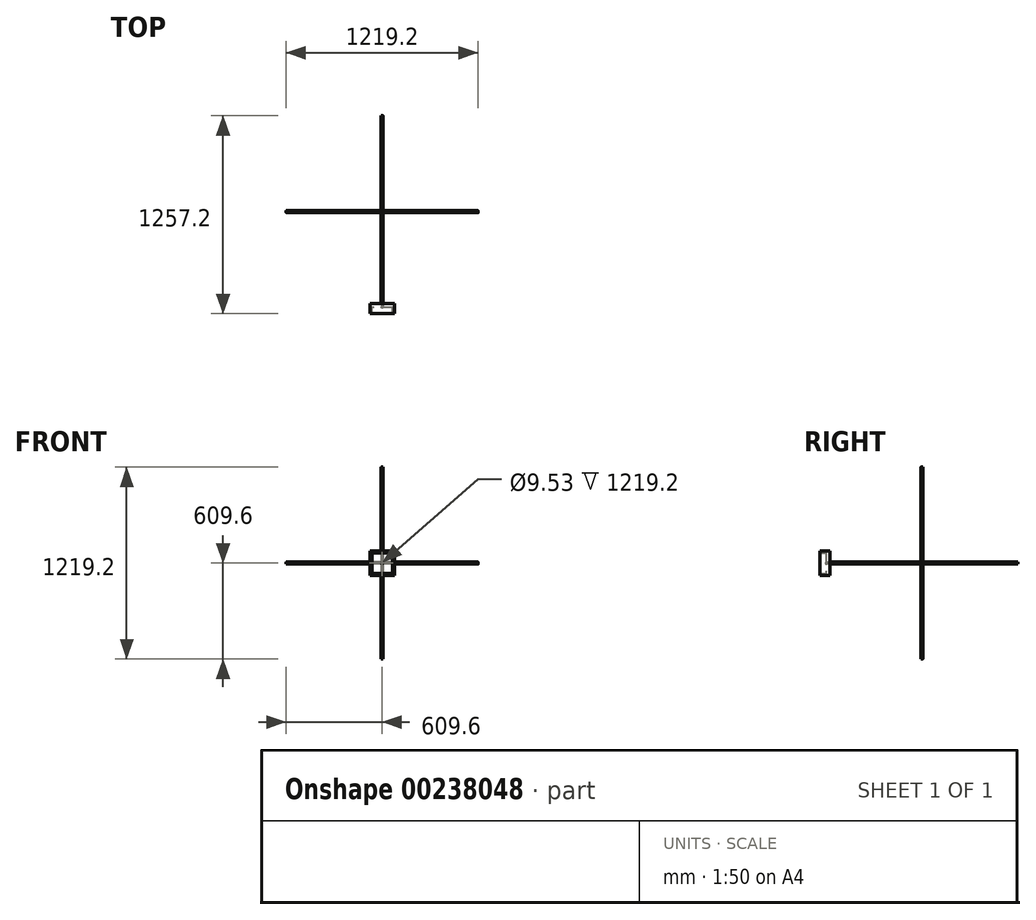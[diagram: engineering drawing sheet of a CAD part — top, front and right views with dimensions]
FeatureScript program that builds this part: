
annotation { "Feature Type Name" : "Feature", "Feature Type Description" : "" }
export const myFeature = defineFeature(function(context is Context, id is Id, definition is map)
    precondition{}
    {
        {
            assignVariable(context, id + "F0", {"name" : "l", "anyValue" : 1219.2 * mm});
        }
        {
            var Q0;
            Q0=qCreatedBy(makeId("Top.planeOp"),FACE);
            var sketch = newSketch(context, id + "F1", { "sketchPlane" : qUnion([Q0])});
            skCircle(sketch, "E0", {"center": v(0, 0) * mm, "radius": 6.35 * mm});
            skSolve(sketch);
        }
        {
            var Q0;
            Q0=qCreatedBy(makeId("Front.planeOp"),FACE);
            var sketch = newSketch(context, id + "F2", { "sketchPlane" : qUnion([Q0])});
            skCircle(sketch, "E1", {"center": v(0, 0) * mm, "radius": 6.35 * mm});
            skSolve(sketch);
        }
        {
            var Q0;
            Q0=qCreatedBy(makeId("Right.planeOp"),FACE);
            var sketch = newSketch(context, id + "F3", { "sketchPlane" : qUnion([Q0])});
            skCircle(sketch, "E2", {"center": v(0, 0) * mm, "radius": 6.35 * mm});
            skSolve(sketch);
        }
        {
            var Q0;
            Q0=makeQuery(id+"F2.imprint","IMPRINT",FACE,{"disambiguationData":[TD([[makeQuery(id+"F2.imprint","IMPRINT",EDGE,{"derivedFrom":sQuery(id+"F2.wireOp",EDGE,"E1")}),1.0]])]});
            extrude(context, id + "F4", {"entities" : qUnion([Q0]), "endBound" : BoundingType.SYMMETRIC, "depth" : getVariable(context, 'l')});
        }
        {
            var Q0;
            Q0=makeQuery(id+"F3.imprint","IMPRINT",FACE,{"disambiguationData":[TD([[makeQuery(id+"F3.imprint","IMPRINT",EDGE,{"derivedFrom":sQuery(id+"F3.wireOp",EDGE,"E2")}),1.0]])]});
            extrude(context, id + "F5", {"entities" : qUnion([Q0]), "operationType" : NewBodyOperationType.ADD, "endBound" : BoundingType.SYMMETRIC, "depth" : getVariable(context, 'l')});
        }
        {
            var Q0;
            Q0=makeQuery(id+"F1.imprint","IMPRINT",FACE,{"disambiguationData":[TD([[makeQuery(id+"F1.imprint","IMPRINT",EDGE,{"derivedFrom":sQuery(id+"F1.wireOp",EDGE,"E0")}),1.0]])]});
            extrude(context, id + "F6", {"entities" : qUnion([Q0]), "operationType" : NewBodyOperationType.ADD, "endBound" : BoundingType.SYMMETRIC, "depth" : getVariable(context, 'l')});
        }
        {
            var Q0;
            Q0=makeQuery(id+"F4.opExtrude","CAP_FACE",FACE,{"disambiguationData":[OSD([sQuery(id+"F2.wireOp",EDGE,"E1")])],"isStart":false});
            var sketch = newSketch(context, id + "F7", { "sketchPlane" : qUnion([Q0])});
            skLineSegment(sketch, "E3.bottom", {"start": v(77.78, 77.78) * mm, "end": v(-77.78, 77.78) * mm});
            skLineSegment(sketch, "E3.top", {"start": v(77.78, -77.78) * mm, "end": v(-77.78, -77.78) * mm});
            skLineSegment(sketch, "E3.left", {"start": v(77.78, 77.78) * mm, "end": v(77.78, -77.78) * mm});
            skLineSegment(sketch, "E3.right", {"start": v(-77.78, 77.78) * mm, "end": v(-77.78, -77.78) * mm});
            skPoint(sketch, "E3.middle", {"position": v(0, 0) * mm});
            skSolve(sketch);
        }
        {
            var Q0;
            Q0 = qSketchRegion(id + "F7", true);
            extrude(context, id + "F8", {"entities" : qUnion([Q0]), "operationType" : NewBodyOperationType.ADD, "oppositeDirection" : true, "depth" : 25.4 * mm});
        }
        {
            var Q0;
            Q0=makeQuery(id+"F8.boolean.opBoolean","MERGE",FACE,{"derivedFrom":[makeQuery(id+"F4.opExtrude","CAP_FACE",FACE,{"disambiguationData":[OSD([sQuery(id+"F2.wireOp",EDGE,"E1")])],"isStart":false}),makeQuery(id+"F8.opExtrude","CAP_FACE",FACE,{"disambiguationData":[OSD([sQuery(id+"F7.wireOp",EDGE,"E3.bottom"),sQuery(id+"F7.wireOp",EDGE,"E3.top"),sQuery(id+"F7.wireOp",EDGE,"E3.left"),sQuery(id+"F7.wireOp",EDGE,"E3.right")])],"isStart":true})]});
            var sketch = newSketch(context, id + "F9", { "sketchPlane" : qUnion([Q0])});
            skLineSegment(sketch, "E4.bottom", {"start": v(65.08, 65.08) * mm, "end": v(-65.08, 65.08) * mm});
            skLineSegment(sketch, "E4.top", {"start": v(65.08, -65.08) * mm, "end": v(-65.08, -65.08) * mm});
            skLineSegment(sketch, "E4.left", {"start": v(65.08, 65.08) * mm, "end": v(65.08, -65.08) * mm});
            skLineSegment(sketch, "E4.right", {"start": v(-65.08, 65.08) * mm, "end": v(-65.08, -65.08) * mm});
            skPoint(sketch, "E4.middle", {"position": v(0, 0) * mm});
            skSolve(sketch);
        }
        {
            assignVariable(context, id + "F10", {"name" : "comFanWallh", "anyValue" : 38 * mm});
        }
        {
            var Q0;
            Q0=makeQuery(id+"F9.imprint","IMPRINT",FACE,{"disambiguationData":[TD([[makeQuery(id+"F9.imprint","IMPRINT",EDGE,{"derivedFrom":sQuery(id+"F9.wireOp",EDGE,"E4.bottom")}),-1.0]])]});
            extrude(context, id + "F11", {"entities" : qUnion([Q0]), "operationType" : NewBodyOperationType.ADD, "depth" : getVariable(context, 'comFanWallh')});
        }
        {
            var Q0;
            Q0=makeQuery(id+"F8.boolean.opBoolean","MERGE",FACE,{"derivedFrom":[makeQuery(id+"F4.opExtrude","CAP_FACE",FACE,{"disambiguationData":[OSD([sQuery(id+"F2.wireOp",EDGE,"E1")])],"isStart":false}),makeQuery(id+"F8.opExtrude","CAP_FACE",FACE,{"disambiguationData":[OSD([sQuery(id+"F7.wireOp",EDGE,"E3.bottom"),sQuery(id+"F7.wireOp",EDGE,"E3.top"),sQuery(id+"F7.wireOp",EDGE,"E3.left"),sQuery(id+"F7.wireOp",EDGE,"E3.right")])],"isStart":true})]});
            var sketch = newSketch(context, id + "F12", { "sketchPlane" : qUnion([Q0])});
            skCircle(sketch, "E5", {"center": v(0, 0) * mm, "radius": 4.76 * mm});
            skSolve(sketch);
        }
        {
            var Q0;
            Q0 = qSketchRegion(id + "F12", true);
            extrude(context, id + "F13", {"entities" : qUnion([Q0]), "operationType" : NewBodyOperationType.REMOVE, "oppositeDirection" : true, "depth" : getVariable(context, 'l')});
        }
    });
